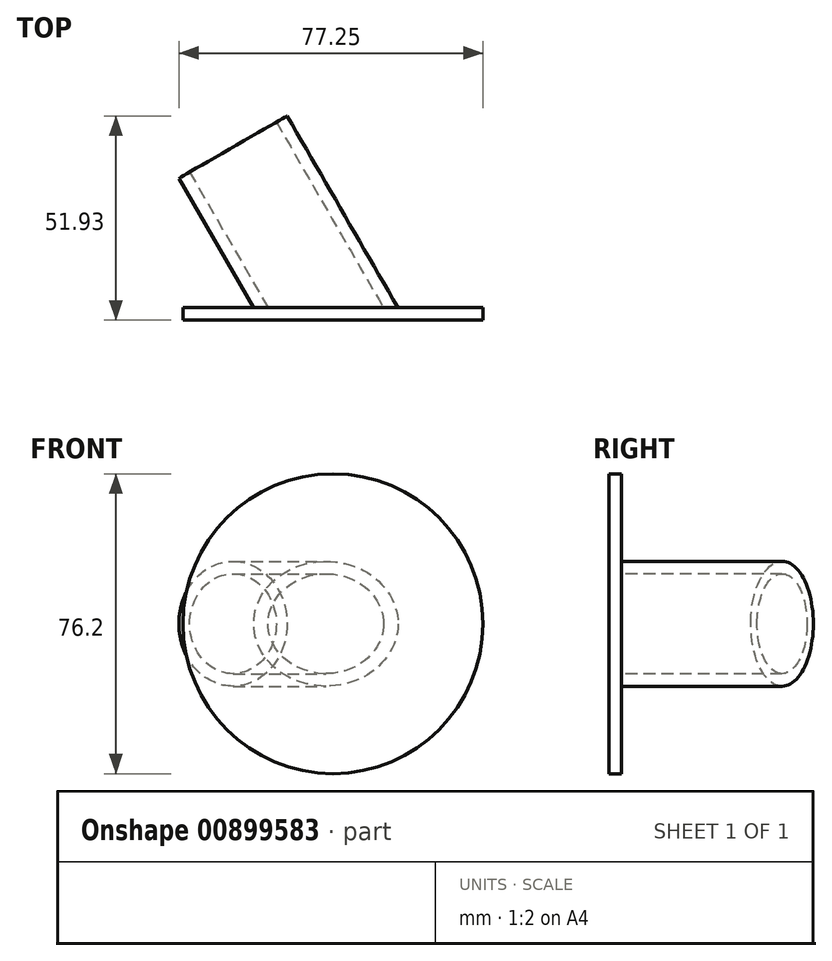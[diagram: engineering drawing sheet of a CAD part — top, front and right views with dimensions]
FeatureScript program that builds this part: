
annotation { "Feature Type Name" : "Feature", "Feature Type Description" : "" }
export const myFeature = defineFeature(function(context is Context, id is Id, definition is map)
    precondition{}
    {
        {
            var Q0;
            Q0=qCreatedBy(makeId("Top.planeOp"),FACE);
            var sketch = newSketch(context, id + "F0", { "sketchPlane" : qUnion([Q0])});
            skLineSegment(sketch, "E0", {"start": v(-53.26, 0) * mm, "end": v(35.2, 0) * mm});
            skSolve(sketch);
        }
        {
            var Q0;
            Q0=sQuery(id+"F0.wireOp",EDGE,"E0");
            cPlane(context, id + "F1", {"entities" : qUnion([Q0]), "cplaneType" : CPlaneType.LINE_ANGLE, "offset" : 25.4 * mm, "angle" : 0 * degree, "width" : 152.4 * mm, "height" : 152.4 * mm});
        }
        {
            var Q0;
            Q0=qCreatedBy(id+"F1.planeOp",FACE);
            var sketch = newSketch(context, id + "F2", { "sketchPlane" : qUnion([Q0])});
            skCircle(sketch, "E1", {"center": v(0, 0) * mm, "radius": 38.1 * mm});
            skSolve(sketch);
        }
        {
            var Q0;
            Q0=makeQuery(id+"F2.imprint","IMPRINT",FACE,{"disambiguationData":[TD([[makeQuery(id+"F2.imprint","IMPRINT",EDGE,{"derivedFrom":sQuery(id+"F2.wireOp",EDGE,"E1")}),1.0]])]});
            extrude(context, id + "F3", {"entities" : qUnion([Q0]), "depth" : 3.17 * mm, "offsetDistance" : 25.4 * mm});
        }
        {
            var Q0;
            Q0=qCreatedBy(id+"F1.planeOp",FACE);
            var sketch = newSketch(context, id + "F4", { "sketchPlane" : qUnion([Q0])});
            skLineSegment(sketch, "E2", {"start": v(0, 0) * mm, "end": v(0, -23.54) * mm});
            skSolve(sketch);
        }
        {
            var Q0;
            Q0=sQuery(id+"F4.wireOp",EDGE,"E2");
            cPlane(context, id + "F5", {"entities" : qUnion([Q0]), "cplaneType" : CPlaneType.LINE_ANGLE, "offset" : 25.4 * mm, "angle" : 60 * degree, "width" : 152.4 * mm, "height" : 152.4 * mm});
        }
        {
            var Q0;
            Q0=qCreatedBy(id+"F5.planeOp",FACE);
            var sketch = newSketch(context, id + "F6", { "sketchPlane" : qUnion([Q0])});
            skCircle(sketch, "E3", {"center": v(0, 0) * mm, "radius": 15.88 * mm});
            skCircle(sketch, "E4", {"center": v(0, 0) * mm, "radius": 12.7 * mm});
            skSolve(sketch);
        }
        {
            var Q0;
            Q0 = qSketchRegion(id + "F6", true);
            extrude(context, id + "F7", {"entities" : qUnion([Q0]), "operationType" : NewBodyOperationType.ADD, "depth" : 50.8 * mm, "offsetDistance" : 25.4 * mm, "hasSecondDirection" : true, "secondDirectionOppositeDirection" : true, "secondDirectionDepth" : 6.35 * mm});
        }
        {
            var Q0;
            Q0=qCreatedBy(makeId("Right.planeOp"),FACE);
            var sketch = newSketch(context, id + "F8", { "sketchPlane" : qUnion([Q0])});
            skLineSegment(sketch, "E5", {"start": v(0, 23.29) * mm, "end": v(0, -20.3) * mm});
            skLineSegment(sketch, "E6", {"start": v(0, -20.3) * mm, "end": v(-8.3, -22.63) * mm});
            skLineSegment(sketch, "E7", {"start": v(-8.3, -22.63) * mm, "end": v(-20.02, 19.2) * mm});
            skLineSegment(sketch, "E8", {"start": v(-20.02, 19.2) * mm, "end": v(0, 23.29) * mm});
            skSolve(sketch);
        }
        {
            var Q0;
            Q0=makeQuery(id+"F8.imprint","IMPRINT",FACE,{"disambiguationData":[TD([[makeQuery(id+"F8.imprint","IMPRINT",EDGE,{"derivedFrom":sQuery(id+"F8.wireOp",EDGE,"E5")}),-1.0]])]});
            extrude(context, id + "F9", {"entities" : qUnion([Q0]), "operationType" : NewBodyOperationType.REMOVE, "oppositeDirection" : true, "depth" : 25.4 * mm, "offsetDistance" : 25.4 * mm, "hasSecondDirection" : true, "secondDirectionOppositeDirection" : false, "secondDirectionDepth" : 25.4 * mm});
        }
    });
